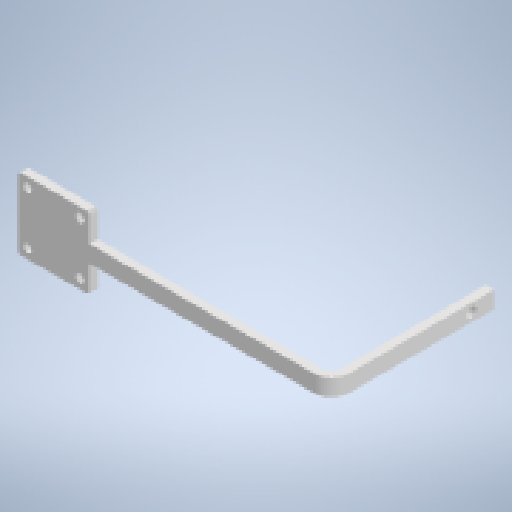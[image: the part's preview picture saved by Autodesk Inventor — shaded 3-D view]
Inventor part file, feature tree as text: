
AUTODESK INVENTOR PART (.ipt)
format: ipt  version: 2023 (Build 270158000, 158)  size: 192,000 bytes
history: native  units: mm
features: reference x12, other x5, sheet_metal_op x3, sketch x2
ambient origin geometry x8: Origin, YZ Plane, XZ Plane, XY Plane, X Axis, Y Axis, Z Axis, Center Point
bodies: Solid1 (feature_tree)
feature tree (22):
  sheet_metal_op  "Face1"
  sheet_metal_op  "Face2"
  sketch  "Sketch1"  dims[d0=2.0mm]
  reference  "Reference1"
  reference  "Reference2"
  reference  "Reference3"
  reference  "Reference4"
  reference  "Reference5"
  reference  "Reference6"
  reference  "Reference7"
  reference  "Reference8"
  reference  "Reference9"
  reference  "Reference10"
  reference  "Reference11"
  other  "Plate1"
  sketch  "Sketch2"  dims[d1=10.0mm d2=5.0mm d3=5.0mm d4=5.5mm d5=5.0mm d6=5.0mm d7=2.5mm d8=10.0mm d9=5.0mm]
  reference  "Reference12"
  other  "Plate2"
  sheet_metal_op  "Bend1"
  other  "ensamble_general.iam"
  other  "stepper:1"
  other  "sostenedor_part1:1"
